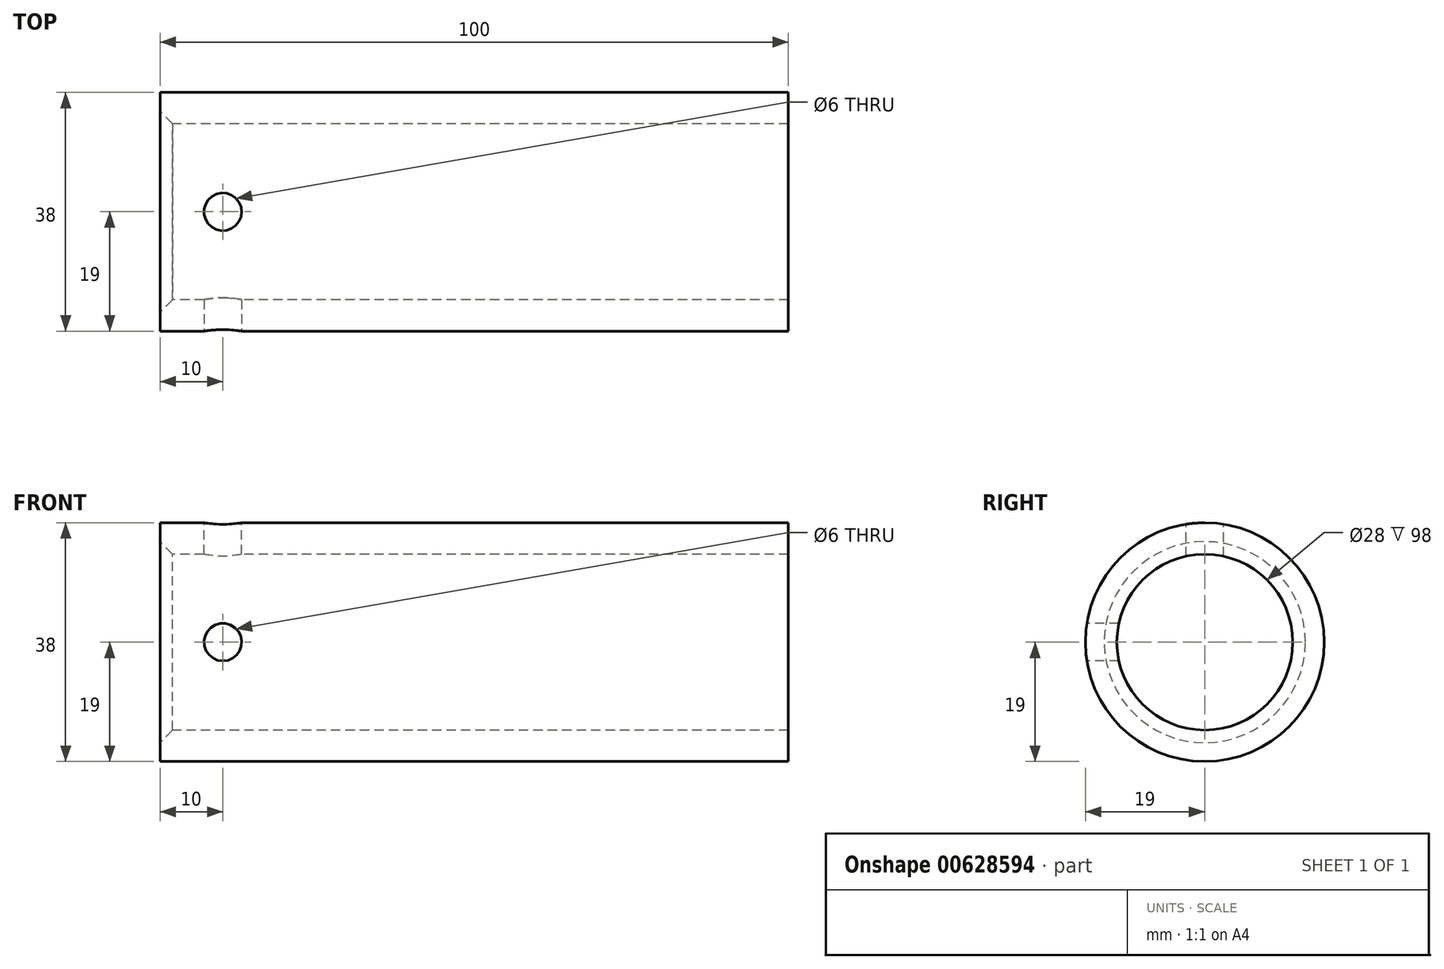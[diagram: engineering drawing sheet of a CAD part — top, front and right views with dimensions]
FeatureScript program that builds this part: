
annotation { "Feature Type Name" : "Feature", "Feature Type Description" : "" }
export const myFeature = defineFeature(function(context is Context, id is Id, definition is map)
    precondition{}
    {
        {
            var Q0;
            Q0=qCreatedBy(makeId("Right.planeOp"),FACE);
            var sketch = newSketch(context, id + "F0", { "sketchPlane" : qUnion([Q0])});
            skCircle(sketch, "E0", {"center": v(0, 0) * mm, "radius": 19 * mm});
            skCircle(sketch, "E1", {"center": v(0, 0) * mm, "radius": 14 * mm});
            skSolve(sketch);
        }
        {
            var Q0;
            Q0=makeQuery(id+"F0.imprint","IMPRINT",FACE,{"disambiguationData":[TD([[makeQuery(id+"F0.imprint","IMPRINT",EDGE,{"derivedFrom":sQuery(id+"F0.wireOp",EDGE,"E0")}),1.0]])]});
            extrude(context, id + "F1", {"entities" : qUnion([Q0]), "depth" : 100 * mm, "offsetDistance" : 25 * mm});
        }
        {
            var Q0;
            Q0=makeQuery(id+"F1.opExtrude","CAP_EDGE",EDGE,{"disambiguationData":[OSD([sQuery(id+"F0.wireOp",EDGE,"E1")])],"isStart":true});
            chamfer(context, id + "F2", {"entities" : qUnion([Q0]), "chamferType" : ChamferType.OFFSET_ANGLE, "width" : 2 * mm, "oppositeDirection" : true, "angle" : 45 * degree, "tangentPropagation" : true});
        }
        {
            var Q0;
            Q0=qCreatedBy(makeId("Top.planeOp"),FACE);
            cPlane(context, id + "F3", {"entities" : qUnion([Q0]), "cplaneType" : CPlaneType.OFFSET, "offset" : 19 * mm, "width" : 150 * mm, "height" : 150 * mm});
        }
        {
            var Q0;
            Q0=qCreatedBy(makeId("Front.planeOp"),FACE);
            cPlane(context, id + "F4", {"entities" : qUnion([Q0]), "cplaneType" : CPlaneType.OFFSET, "offset" : 19 * mm, "width" : 150 * mm, "height" : 150 * mm});
        }
        {
            var Q0;
            Q0=qCreatedBy(id+"F3.planeOp",FACE);
            var sketch = newSketch(context, id + "F5", { "sketchPlane" : qUnion([Q0])});
            skCircle(sketch, "E2", {"center": v(10, 0) * mm, "radius": 3 * mm});
            skSolve(sketch);
        }
        {
            var Q0;
            Q0 = qSketchRegion(id + "F5", true);
            extrude(context, id + "F6", {"entities" : qUnion([Q0]), "operationType" : NewBodyOperationType.REMOVE, "endBound" : BoundingType.UP_TO_NEXT, "oppositeDirection" : true, "depth" : 25 * mm, "offsetDistance" : 25 * mm});
        }
        {
            var Q0;
            Q0=qCreatedBy(id+"F4.planeOp",FACE);
            var sketch = newSketch(context, id + "F7", { "sketchPlane" : qUnion([Q0])});
            skCircle(sketch, "E3", {"center": v(10, 0) * mm, "radius": 3 * mm});
            skSolve(sketch);
        }
        {
            var Q0;
            Q0 = qSketchRegion(id + "F7", true);
            extrude(context, id + "F8", {"entities" : qUnion([Q0]), "operationType" : NewBodyOperationType.REMOVE, "endBound" : BoundingType.UP_TO_NEXT, "oppositeDirection" : true, "depth" : 25 * mm, "offsetDistance" : 25 * mm});
        }
    });
